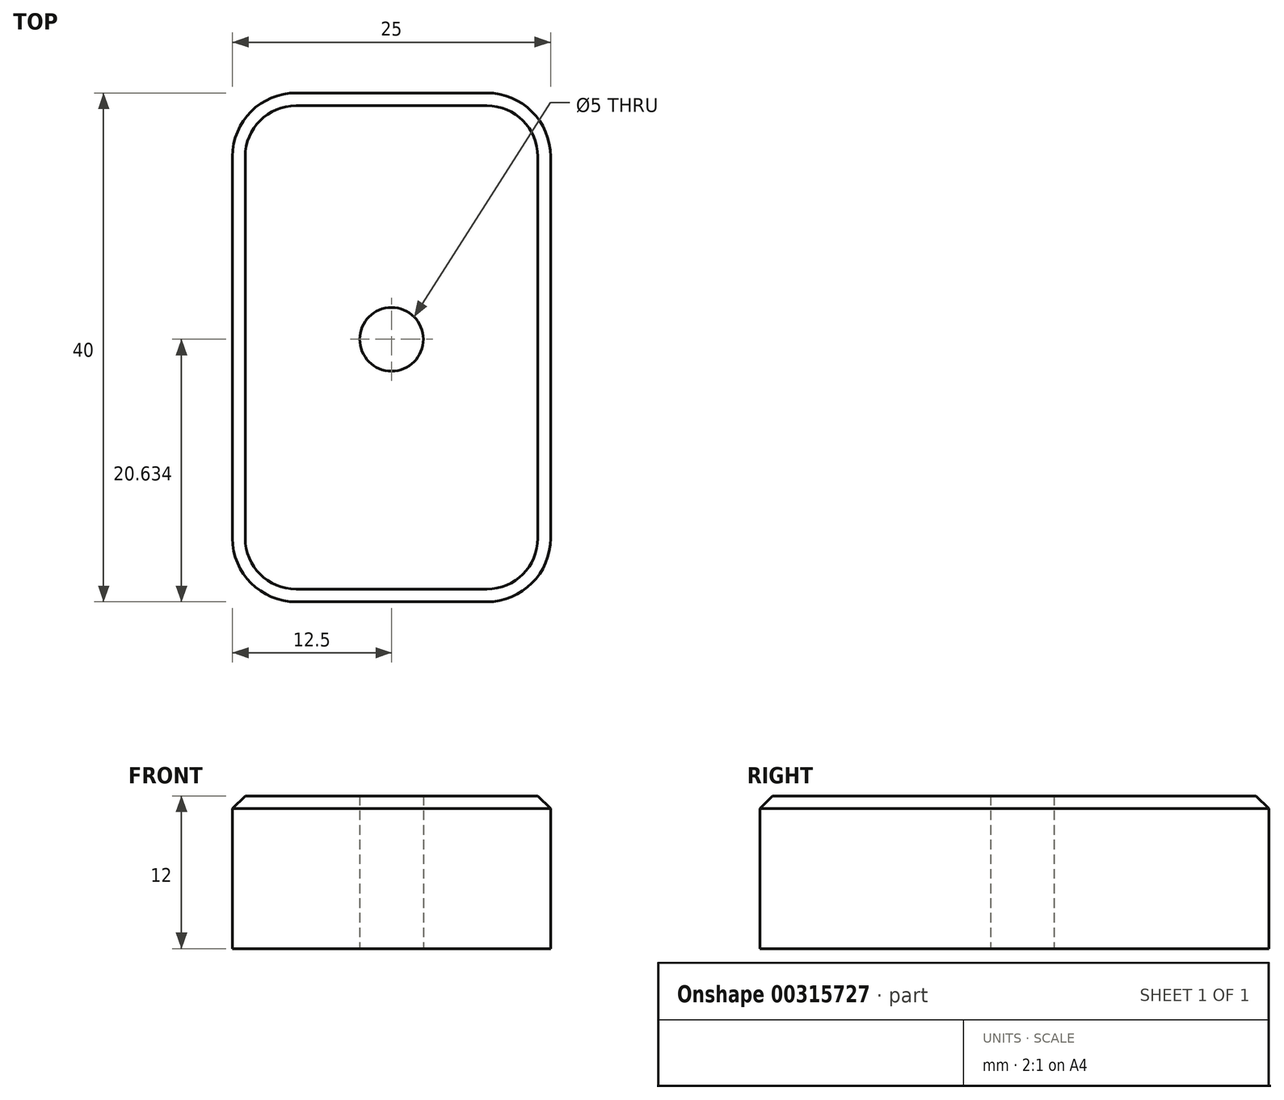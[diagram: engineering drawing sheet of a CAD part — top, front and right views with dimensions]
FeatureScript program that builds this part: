
annotation { "Feature Type Name" : "Feature", "Feature Type Description" : "" }
export const myFeature = defineFeature(function(context is Context, id is Id, definition is map)
    precondition{}
    {
        {
            var Q0;
            Q0=qCreatedBy(makeId("Top.planeOp"),FACE);
            var sketch = newSketch(context, id + "F0", { "sketchPlane" : qUnion([Q0])});
            skLineSegment(sketch, "E0.bottom", {"start": v(-12.5, 20) * mm, "end": v(12.5, 20) * mm});
            skLineSegment(sketch, "E0.top", {"start": v(-12.5, -20) * mm, "end": v(12.5, -20) * mm});
            skLineSegment(sketch, "E0.left", {"start": v(-12.5, 20) * mm, "end": v(-12.5, -20) * mm});
            skLineSegment(sketch, "E0.right", {"start": v(12.5, 20) * mm, "end": v(12.5, -20) * mm});
            skPoint(sketch, "E0.middle", {"position": v(0, 0) * mm});
            skSolve(sketch);
        }
        {
            var Q0;
            Q0 = qSketchRegion(id + "F0", true);
            extrude(context, id + "F1", {"entities" : qUnion([Q0]), "depth" : 12 * mm});
        }
        {
            var Q0;
            Q0=makeQuery(id+"F1.opExtrude","CAP_FACE",FACE,{"disambiguationData":[OSD([sQuery(id+"F0.wireOp",EDGE,"E0.bottom"),sQuery(id+"F0.wireOp",EDGE,"E0.top"),sQuery(id+"F0.wireOp",EDGE,"E0.left"),sQuery(id+"F0.wireOp",EDGE,"E0.right")])],"isStart":true});
            var sketch = newSketch(context, id + "F2", { "sketchPlane" : qUnion([Q0])});
            skCircle(sketch, "E1", {"center": v(0, -0.63) * mm, "radius": 2.5 * mm});
            skSolve(sketch);
        }
        {
            var Q0;
            Q0 = qSketchRegion(id + "F2", true);
            extrude(context, id + "F3", {"entities" : qUnion([Q0]), "operationType" : NewBodyOperationType.REMOVE, "oppositeDirection" : true, "depth" : 123.8 * mm});
        }
        {
            var Q0;
            Q0=makeQuery(id+"F1.opExtrude","SWEPT_EDGE",EDGE,{"disambiguationData":[OSD([sQuery(id+"F0.wireOp",EDGE,"E0.top"),sQuery(id+"F0.wireOp",EDGE,"E0.left")])]});
            fillet(context, id + "F4", {"entities" : qUnion([Q0]), "radius" : 5 * mm, "tangentPropagation" : true, "allowEdgeOverflow" : false});
        }
        {
            var Q0;
            Q0=makeQuery(id+"F1.opExtrude","SWEPT_EDGE",EDGE,{"disambiguationData":[OSD([sQuery(id+"F0.wireOp",EDGE,"E0.top"),sQuery(id+"F0.wireOp",EDGE,"E0.right")])]});
            fillet(context, id + "F5", {"entities" : qUnion([Q0]), "radius" : 5 * mm, "tangentPropagation" : true, "allowEdgeOverflow" : false});
        }
        {
            var Q0;
            Q0=makeQuery(id+"F1.opExtrude","SWEPT_EDGE",EDGE,{"disambiguationData":[OSD([sQuery(id+"F0.wireOp",EDGE,"E0.bottom"),sQuery(id+"F0.wireOp",EDGE,"E0.left")])]});
            fillet(context, id + "F6", {"entities" : qUnion([Q0]), "radius" : 5 * mm, "tangentPropagation" : true, "allowEdgeOverflow" : false});
        }
        {
            var Q0;
            Q0=makeQuery(id+"F1.opExtrude","SWEPT_EDGE",EDGE,{"disambiguationData":[OSD([sQuery(id+"F0.wireOp",EDGE,"E0.bottom"),sQuery(id+"F0.wireOp",EDGE,"E0.right")])]});
            fillet(context, id + "F7", {"entities" : qUnion([Q0]), "radius" : 5 * mm, "tangentPropagation" : true, "allowEdgeOverflow" : false});
        }
        {
            var Q0;
            Q0=makeQuery(id+"F1.opExtrude","CAP_EDGE",EDGE,{"disambiguationData":[OSD([sQuery(id+"F0.wireOp",EDGE,"E0.bottom")])],"isStart":false});
            chamfer(context, id + "F8", {"entities" : qUnion([Q0]), "width" : 1 * mm, "tangentPropagation" : true});
        }
    });
